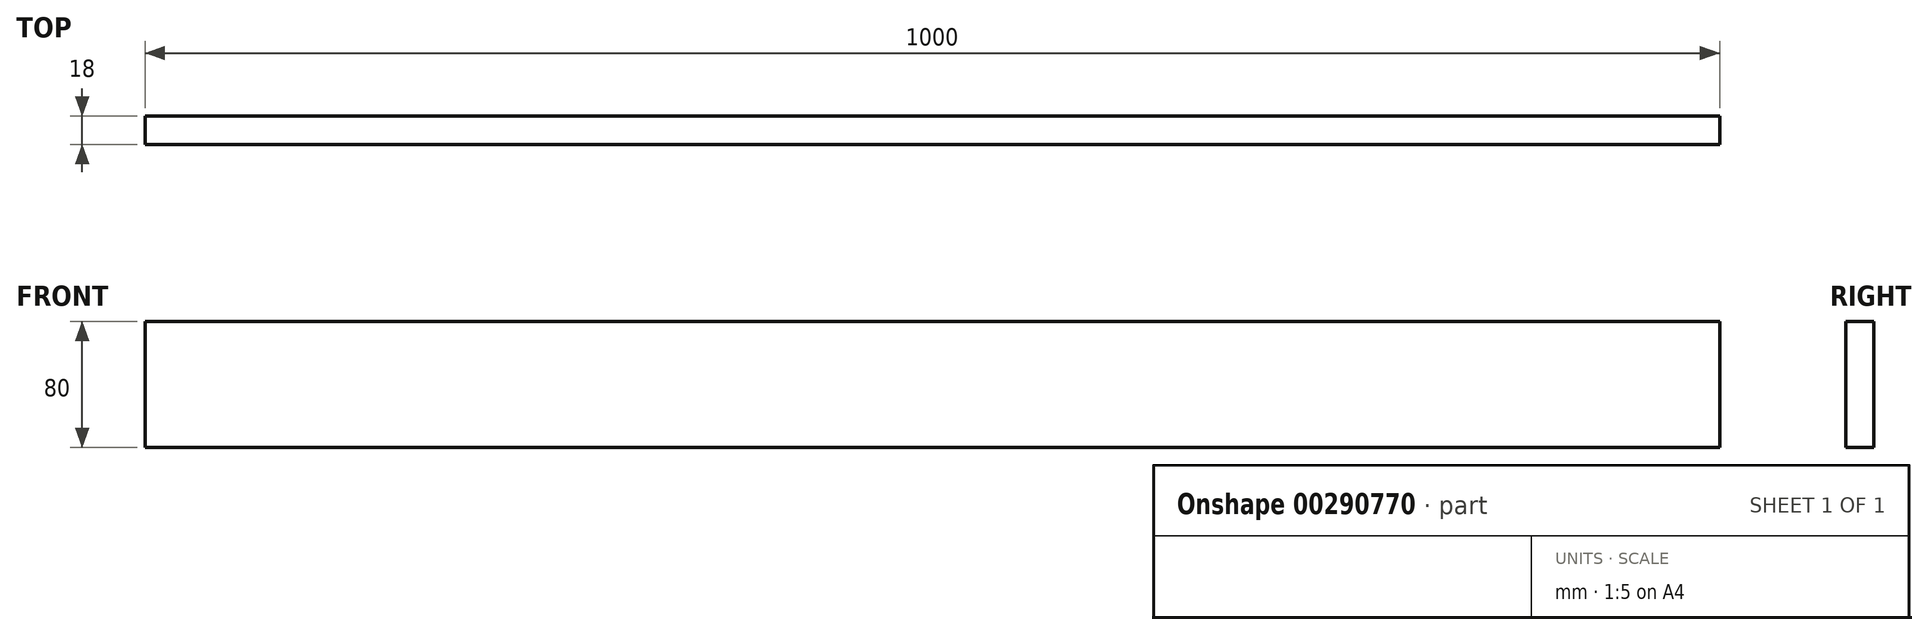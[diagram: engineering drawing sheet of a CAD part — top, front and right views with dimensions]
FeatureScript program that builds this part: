
annotation { "Feature Type Name" : "Feature", "Feature Type Description" : "" }
export const myFeature = defineFeature(function(context is Context, id is Id, definition is map)
    precondition{}
    {
        {
            var Q0;
            Q0=qCreatedBy(makeId("Front.planeOp"),FACE);
            var sketch = newSketch(context, id + "F0", { "sketchPlane" : qUnion([Q0])});
            skLineSegment(sketch, "E0.bottom", {"start": v(0, 0) * mm, "end": v(1000, 0) * mm});
            skLineSegment(sketch, "E0.top", {"start": v(0, 80) * mm, "end": v(1000, 80) * mm});
            skLineSegment(sketch, "E0.left", {"start": v(0, 0) * mm, "end": v(0, 80) * mm});
            skLineSegment(sketch, "E0.right", {"start": v(1000, 0) * mm, "end": v(1000, 80) * mm});
            skSolve(sketch);
        }
        {
            var Q0;
            Q0 = qSketchRegion(id + "F0", true);
            extrude(context, id + "F1", {"entities" : qUnion([Q0]), "depth" : 18 * mm});
        }
    });
